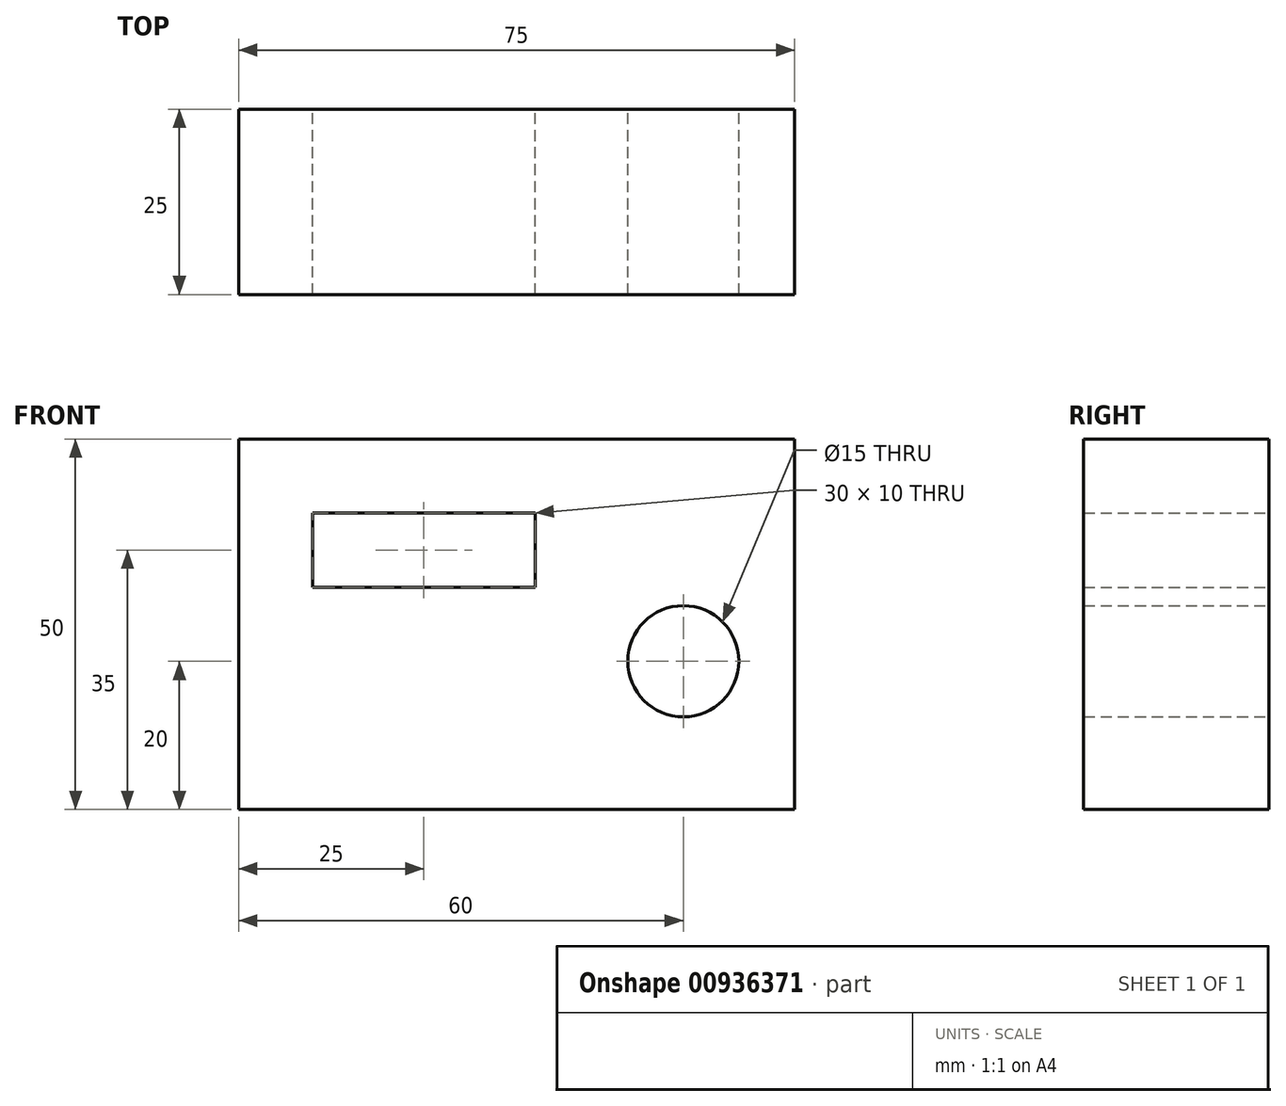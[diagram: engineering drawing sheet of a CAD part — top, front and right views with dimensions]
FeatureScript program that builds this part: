
annotation { "Feature Type Name" : "Feature", "Feature Type Description" : "" }
export const myFeature = defineFeature(function(context is Context, id is Id, definition is map)
    precondition{}
    {
        {
            var Q0;
            Q0=qCreatedBy(makeId("Front.planeOp"),FACE);
            var sketch = newSketch(context, id + "F0", { "sketchPlane" : qUnion([Q0])});
            skLineSegment(sketch, "E0", {"start": v(0, 0) * mm, "end": v(15, 0) * mm});
            skLineSegment(sketch, "E1", {"start": v(15, 0) * mm, "end": v(15, -20) * mm});
            skLineSegment(sketch, "E2", {"start": v(15, -20) * mm, "end": v(0, -20) * mm});
            skLineSegment(sketch, "E3", {"start": v(0, -20) * mm, "end": v(0, 0) * mm});
            skLineSegment(sketch, "E4", {"start": v(0, -20) * mm, "end": v(-60, -20) * mm});
            skLineSegment(sketch, "E5", {"start": v(-60, -20) * mm, "end": v(-60, 30) * mm});
            skLineSegment(sketch, "E6", {"start": v(-60, 30) * mm, "end": v(15, 30) * mm});
            skLineSegment(sketch, "E7", {"start": v(15, 30) * mm, "end": v(15, 0) * mm});
            skCircle(sketch, "E8", {"center": v(0, 0) * mm, "radius": 7.5 * mm});
            skLineSegment(sketch, "E9", {"start": v(-50, 30) * mm, "end": v(-50, 20) * mm});
            skLineSegment(sketch, "E10", {"start": v(-50, 20) * mm, "end": v(-60, 20) * mm});
            skLineSegment(sketch, "E11", {"start": v(-50, 20) * mm, "end": v(-20, 20) * mm});
            skLineSegment(sketch, "E12", {"start": v(-20, 20) * mm, "end": v(-20, 10) * mm});
            skLineSegment(sketch, "E13", {"start": v(-20, 10) * mm, "end": v(-50, 10) * mm});
            skLineSegment(sketch, "E14", {"start": v(-50, 10) * mm, "end": v(-50, 20) * mm});
            skSolve(sketch);
        }
        {
            var Q0;
            {var subQ4=sQuery(id+"F0.wireOp",EDGE,"E9");Q0=makeQuery(id+"F0.imprint","IMPRINT",FACE,{"disambiguationData":[TD([[makeQuery(id+"F0.imprint","IMPRINT",EDGE,{"derivedFrom":subQ4}),-1.0]])]});}
            var Q1;
            {var subQ4=sQuery(id+"F0.wireOp",EDGE,"E1");Q1=makeQuery(id+"F0.imprint","IMPRINT",FACE,{"disambiguationData":[TD([[makeQuery(id+"F0.imprint","IMPRINT",EDGE,{"derivedFrom":subQ4}),-1.0]])]});}
            var Q2;
            {var subQ8=sQuery(id+"F0.wireOp",EDGE,"E4");Q2=makeQuery(id+"F0.imprint","IMPRINT",FACE,{"disambiguationData":[TD([[makeQuery(id+"F0.imprint","IMPRINT",EDGE,{"derivedFrom":subQ8}),-1.0]])]});}
            extrude(context, id + "F1", {"entities" : qUnion([Q0, Q1, Q2]), "depth" : 25 * mm, "offsetDistance" : 25 * mm});
        }
    });
